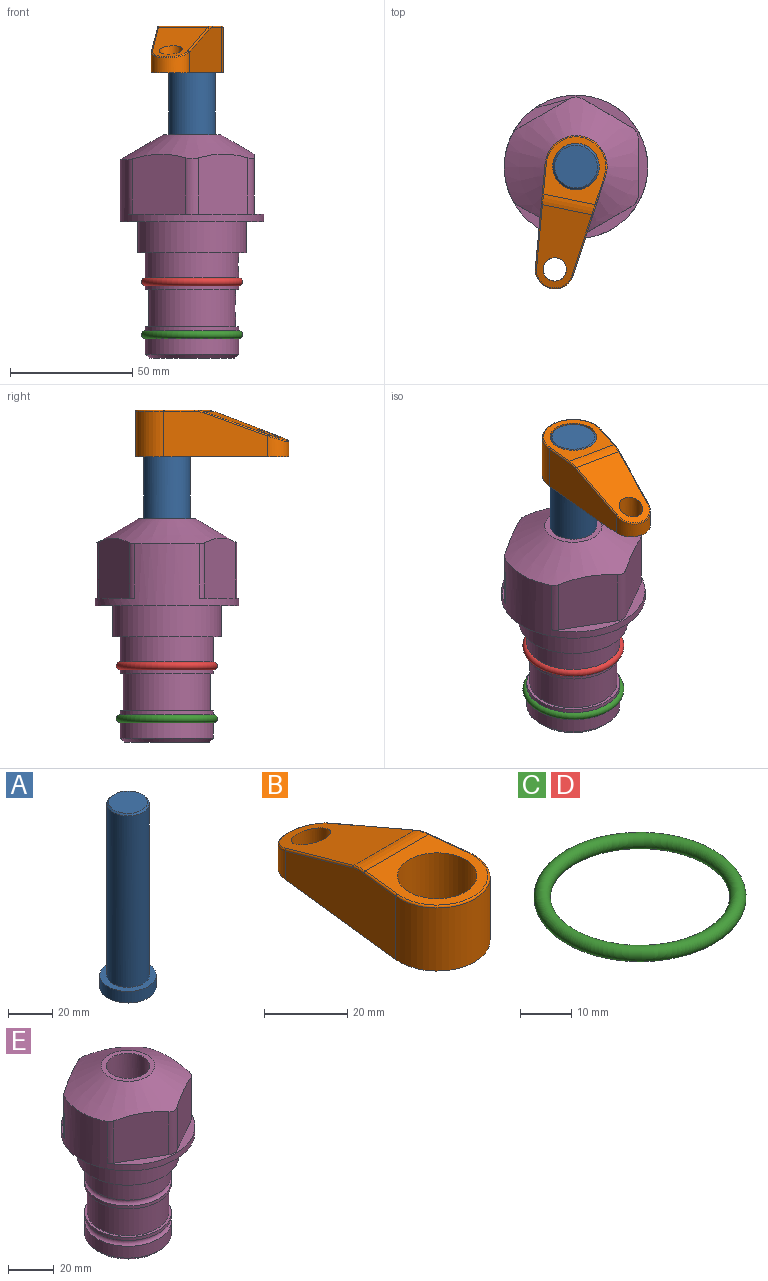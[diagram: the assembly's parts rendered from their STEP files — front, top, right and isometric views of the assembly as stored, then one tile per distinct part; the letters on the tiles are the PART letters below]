
ASSEMBLY  parts=5 mates=3
PART A: 6 faces, bbox 25.4x25.4x101.6 mm
  f0: plane 17.46x17.46mm, normal (0,0,1), area 239.5mm2, adj f5
  f1: plane 25.4x25.4mm, normal (0,0,-1), area 506.7mm2, adj f2
  f2: cylinder r=12.7mm len=25.4mm, axis (0,0,1), area 506.7mm2, adj f1,f3
  f3: plane 25.4x25.4mm, normal (0,0,1), area 221.7mm2, adj f2,f4
  f4: cylinder r=9.53mm len=94.46mm, axis (0,0,1), area 5653mm2, adj f3,f5
  f5: cone r=8.73mm half-angle=45deg, axis (0,0,-1), area 64.4mm2, adj f0,f4
PART B: 44 faces, bbox 27.5x64.5x19.1 mm
  f0: plane 2.3x0.95mm, normal (0,0,-1), area 1mm2, adj f25,f30,f34
  f1: plane 63.5x25.4mm, normal (0,0,-1), area 561.7mm2, adj f2,f3,f4,f5,f6,f7,f19,f20
  f2: cylinder r=12.7mm len=25.4mm, axis (0,0,-1), area 792.2mm2, adj f1,f3,f5,f13
  f3: plane 42.33x18.54mm, normal (0.99,0.11,0), area 647mm2, adj f1,f2,f4,f11,f12,f14
  f4: cylinder r=7.94mm len=15.78mm, axis (0,0,-1), area 158.6mm2, adj f1,f3,f5,f16
  f5: plane 42.33x18.54mm, normal (-0.99,0.11,0), area 647mm2, adj f1,f2,f4,f15,f17,f18
  f6: cylinder r=9.53mm len=19.05mm, axis (0,0,-1), area 1140.1mm2, adj f1,f8
  f7: cylinder r=4.76mm len=10.98mm, axis (0,0,-1), area 276.1mm2, adj f1,f9
  f8: plane 25.83x24.38mm, normal (0,0,1), area 262.2mm2, adj f6,f10,f11,f13,f15
  f9: plane 32.49x20.55mm, normal (0,0.34,0.94), area 489.9mm2, adj f7,f10,f14,f16,f18
  f10: cylinder r=12.7mm len=21.49mm, axis (-1,0,0), area 93.2mm2, adj f8,f9,f12,f17
  f11: cylinder r=0.51mm len=12.34mm, axis (0.11,-0.99,0), area 9.9mm2, adj f3,f8,f12,f13
  f12: bspline ~7.62x1.64mm, area 3.5mm2, adj f3,f10,f11,f14
  f13: torus R=12.19mm, axis (0,0,1), area 33.6mm2, adj f2,f8,f11,f15
  f14: cylinder r=0.51mm len=26.01mm, axis (0.1,-0.93,0.34), area 21.6mm2, adj f3,f9,f12,f16
  f15: cylinder r=0.51mm len=12.34mm, axis (0.11,0.99,0), area 9.9mm2, adj f5,f8,f13,f17
  f16: bspline ~15.78x7.05mm, area 15.7mm2, adj f4,f9,f14,f18
  f17: bspline ~7.62x1.64mm, area 3.5mm2, adj f5,f10,f15,f18
  f18: cylinder r=0.51mm len=26.01mm, axis (0.1,0.93,-0.34), area 21.6mm2, adj f5,f9,f16,f17
  f19: plane 21.6x14.29mm, normal (-0.99,-0.11,0), area 242.6mm2, adj f1,f26,f28,f34,f36,f38
  f20: plane 21.6x14.29mm, normal (0.99,-0.11,0), area 242.6mm2, adj f1,f27,f29,f37,f39,f41
  f21: cylinder r=12.7mm len=14.29mm, axis (0,0,-1), area 173.2mm2, adj f1,f26,f27,f30,f31,f33
  f22: cylinder r=7.94mm len=7.63mm, axis (0,0,-1), area 53.8mm2, adj f1,f28,f29,f42
  f23: plane 2.3x0.95mm, normal (0,0,-1), area 1mm2, adj f25,f33,f37
  f24: plane 17.94x12.32mm, normal (0,-0.34,-0.94), area 191.2mm2, adj f25,f38,f41,f42
  f25: cylinder r=9.53mm len=12.93mm, axis (-1,0,0), area 37.5mm2, adj f0,f23,f24,f31,f36,f39
  f26: cylinder r=1.59mm len=14.29mm, axis (0,0,-1), area 49mm2, adj f1,f19,f21,f32
  f27: cylinder r=1.59mm len=14.29mm, axis (0,0,-1), area 49mm2, adj f1,f20,f21,f35
  f28: cylinder r=1.59mm len=7.28mm, axis (0,0,-1), area 22.1mm2, adj f1,f19,f22,f40
  f29: cylinder r=1.59mm len=7.28mm, axis (0,0,-1), area 22.1mm2, adj f1,f20,f22,f43
  f30: torus R=14.29mm, axis (0,0,1), area 5.8mm2, adj f0,f21,f31,f32
  f31: bspline ~11.06x2.73mm, area 20.8mm2, adj f21,f25,f30,f33
  f32: sphere r=1.59mm, area 5.4mm2, adj f26,f30,f34
  f33: torus R=14.29mm, axis (0,0,1), area 5.8mm2, adj f21,f23,f31,f35
  f34: cylinder r=1.59mm len=1.68mm, axis (-0.11,0.99,0), area 2.4mm2, adj f0,f19,f32,f36
  f35: sphere r=1.59mm, area 5.4mm2, adj f27,f33,f37
  f36: bspline ~5.82x2.33mm, area 7.7mm2, adj f19,f25,f34,f38
  f37: cylinder r=1.59mm len=1.68mm, axis (0.11,0.99,0), area 2.4mm2, adj f20,f23,f35,f39
  f38: cylinder r=1.59mm len=18.33mm, axis (0.1,-0.93,0.34), area 46.7mm2, adj f19,f24,f36,f40
  f39: bspline ~5.82x2.33mm, area 7.7mm2, adj f20,f25,f37,f41
  f40: sphere r=1.59mm, area 3.6mm2, adj f28,f38,f42
  f41: cylinder r=1.59mm len=18.33mm, axis (0.1,0.93,-0.34), area 46.7mm2, adj f20,f24,f39,f43
  f42: bspline ~8.31x1.84mm, area 15.3mm2, adj f22,f24,f40,f43
  f43: sphere r=1.59mm, area 3.6mm2, adj f29,f41,f42
PART C: 1 faces, bbox 44.7x44.7x3.2 mm
  f0: torus R=19.05mm, axis (0,0,1), area 1193.9mm2
PART D: same geometry as C
PART E: 35 faces, bbox 58.7x58.7x91.2 mm
  f0: cylinder r=17.78mm len=35.56mm, axis (0,0,1), area 1670.8mm2, adj f22,f23,f30
  f1: cylinder r=19.05mm len=38.1mm, axis (0,0,1), area 1191.9mm2, adj f25,f26,f29
  f2: plane 24.5x21.62mm, normal (-0.5,0.87,0), area 597.1mm2, adj f9,f10,f15,f16
  f3: cylinder r=29.33mm len=58.66mm, axis (0,0,-1), area 1197.7mm2, adj f8,f9,f10,f11,f16
  f4: plane 24.5x21.62mm, normal (-0.5,-0.87,0), area 597.1mm2, adj f9,f11,f12,f16
  f5: plane 24.5x20.32mm, normal (0.5,-0.87,0), area 562.8mm2, adj f9,f12,f13,f16
  f6: plane 24.5x23.48mm, normal (1,0,0), area 562.8mm2, adj f9,f13,f14,f16
  f7: plane 24.5x20.32mm, normal (0.5,0.87,0), area 562.8mm2, adj f9,f14,f15,f16
  f8: plane 58.66x58.66mm, normal (0,0,-1), area 1150.6mm2, adj f3,f27
  f9: plane 58.66x55.48mm, normal (0,0,1), area 395.6mm2, adj f2,f3,f4,f5,f6,f7,f10,f11
  f10: cylinder r=5.08mm len=22.62mm, axis (0,0,-1), area 65.8mm2, adj f2,f3,f9,f16
  f11: cylinder r=5.08mm len=22.62mm, axis (0,0,-1), area 65.8mm2, adj f3,f4,f9,f16
  f12: cylinder r=5.08mm len=23.01mm, axis (0,0,-1), area 122.4mm2, adj f4,f5,f9,f16
  f13: cylinder r=5.08mm len=23.01mm, axis (0,0,-1), area 122.4mm2, adj f5,f6,f9,f16
  f14: cylinder r=5.08mm len=23.01mm, axis (0,0,-1), area 122.4mm2, adj f6,f7,f9,f16
  f15: cylinder r=5.08mm len=23.01mm, axis (0,0,-1), area 122.4mm2, adj f2,f7,f9,f16
  f16: cone r=11.73mm half-angle=60deg, axis (0,0,-1), area 2163.7mm2, adj f2,f3,f4,f5,f6,f7,f10,f11
  f17: plane 23.46x23.46mm, normal (0,0,1), area 147.4mm2, adj f16,f34
  f18: plane 34.93x34.93mm, normal (0,0,-1), area 958mm2, adj f28
  f19: cylinder r=19.05mm len=38.1mm, axis (0,0,1), area 760.1mm2, adj f20,f28
  f20: torus R=19.05mm, axis (0,0,1), area 565.3mm2, adj f19,f21
  f21: cylinder r=19.05mm len=38.1mm, axis (0,0,1), area 190mm2, adj f20,f22
  f22: plane 38.1x38.1mm, normal (0,0,1), area 146.9mm2, adj f0,f21
  f23: plane 38.1x38.1mm, normal (0,0,-1), area 146.9mm2, adj f0,f24
  f24: cylinder r=19.05mm len=38.1mm, axis (0,0,1), area 190mm2, adj f23,f25
  f25: torus R=19.05mm, axis (0,0,1), area 565.3mm2, adj f1,f24
  f26: plane 44.45x44.45mm, normal (0,0,-1), area 411.7mm2, adj f1,f27
  f27: cylinder r=22.23mm len=44.45mm, axis (0,0,1), area 1773.5mm2, adj f8,f26
  f28: cone r=19.05mm half-angle=45deg, axis (0,0,1), area 257.5mm2, adj f18,f19
  f29: cylinder r=3.17mm len=6.35mm, axis (-1,0,0), area 126.7mm2, adj f1,f32
  f30: cylinder r=3.17mm len=6.35mm, axis (-1,0,0), area 101.3mm2, adj f0,f32
  f31: plane 25.4x25.4mm, normal (0,0,1), area 506.7mm2, adj f32
  f32: cylinder r=12.7mm len=66.42mm, axis (0,0,-1), area 5236.2mm2, adj f29,f30,f31,f33
  f33: cone r=9.53mm half-angle=30deg, axis (0,0,-1), area 443.4mm2, adj f32,f34
  f34: cylinder r=9.53mm len=19.05mm, axis (0,0,-1), area 849mm2, adj f17,f33
PLACE A rot(axis=(0,0,-1),101.7deg) t=(0,0,6.38)mm
PLACE B rot(axis=(0,0,1),168.3deg) t=(0,0,60.99)mm
PLACE C t=(0,0,-21.59)mm
PLACE D at identity
PLACE E at identity fixed
MATE fastened C.f0 <-> E.f0  axis (0,0,1) through (0,0,-46.1)mm
MATE cylindrical A.f2 <-> E.f0  axis (0,0,1) through (0,0,32.01)mm
MATE fastened B.f2 <-> A.f2  axis (0,0,1) through (0,0,80.04)mm
